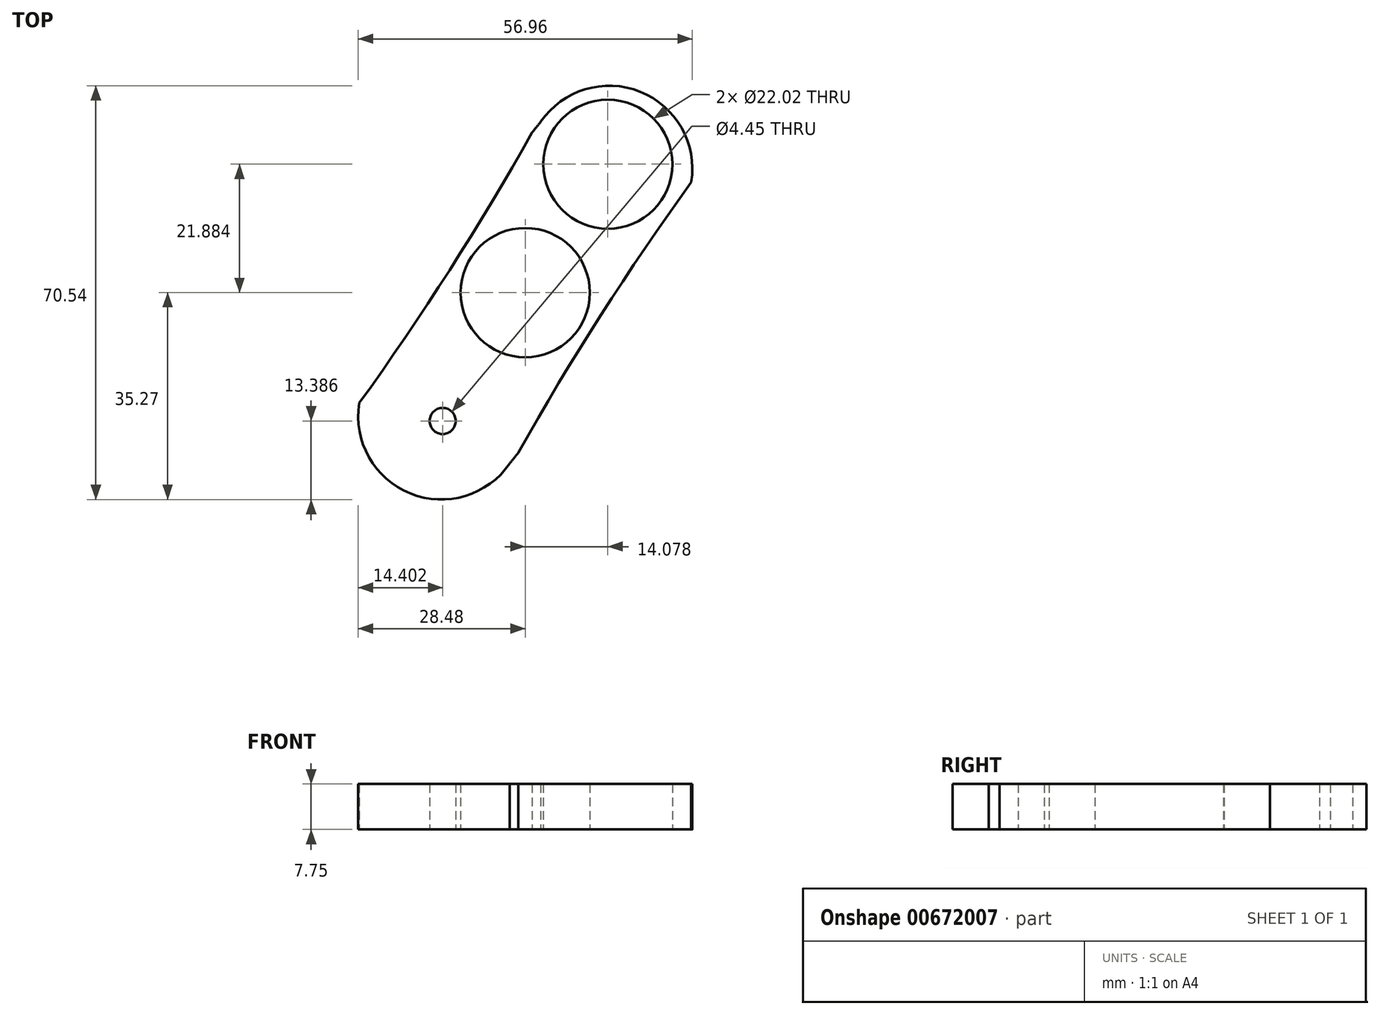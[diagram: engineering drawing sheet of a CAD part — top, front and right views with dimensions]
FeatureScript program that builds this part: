
annotation { "Feature Type Name" : "Feature", "Feature Type Description" : "" }
export const myFeature = defineFeature(function(context is Context, id is Id, definition is map)
    precondition{}
    {
        {
            var Q0;
            Q0=qCreatedBy(makeId("Top.planeOp"),FACE);
            var sketch = newSketch(context, id + "F0", { "sketchPlane" : qUnion([Q0])});
            skCircle(sketch, "E0", {"center": v(0, 0) * mm, "radius": 11.01 * mm});
            skCircle(sketch, "E1", {"center": v(14.08, 21.88) * mm, "radius": 11.01 * mm});
            skArc(sketch, "E2", {"start": v(28.3, 18.82) * mm, "mid": v(19.6, 34.24) * mm, "end": v(2.65, 29.13) * mm});
            skArc(sketch, "E3", {"start": v(28.3, 18.82) * mm, "mid": v(12.9, -3.82) * mm, "end": v(-1.17, -27.3) * mm});
            skArc(sketch, "E4.1.0", {"start": v(-28.3, -18.82) * mm, "mid": v(-19.6, -34.24) * mm, "end": v(-2.65, -29.13) * mm});
            skArc(sketch, "E4.1.1", {"start": v(-28.3, -18.82) * mm, "mid": v(-12.9, 3.82) * mm, "end": v(1.17, 27.3) * mm});
            skArc(sketch, "E5", {"start": v(-1.17, -27.3) * mm, "mid": v(-1.91, -28.21) * mm, "end": v(-2.65, -29.13) * mm});
            skPoint(sketch, "E6.orphan", {"position": v(-4.04, -32.48) * mm});
            skArc(sketch, "E7.1.0", {"start": v(1.17, 27.3) * mm, "mid": v(1.91, 28.21) * mm, "end": v(2.65, 29.13) * mm});
            skPoint(sketch, "E8.orphan", {"position": v(4.04, 32.48) * mm});
            skCircle(sketch, "E9", {"center": v(-14.08, -21.88) * mm, "radius": 2.22 * mm});
            skSolve(sketch);
        }
        {
            var Q0;
            Q0 = qSketchRegion(id + "F0", true);
            extrude(context, id + "F1", {"entities" : qUnion([Q0]), "depth" : 7.75 * mm, "offsetDistance" : 25.4 * mm});
        }
    });
